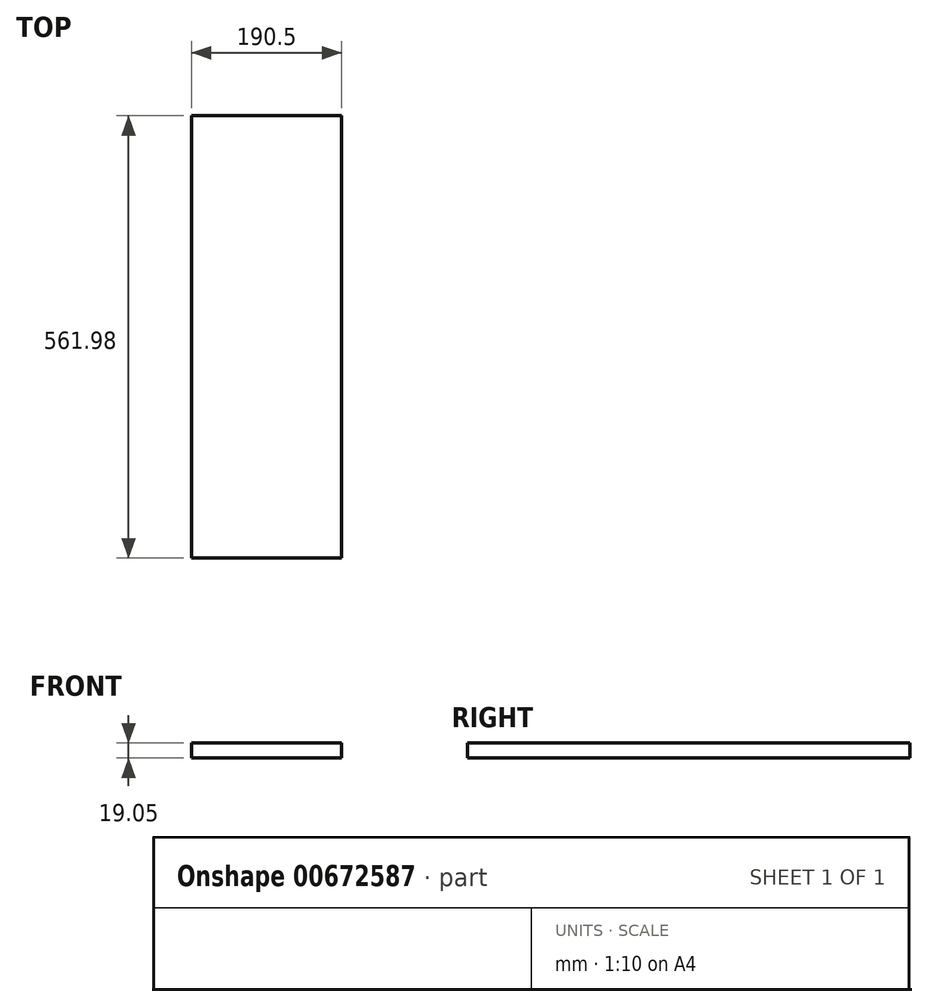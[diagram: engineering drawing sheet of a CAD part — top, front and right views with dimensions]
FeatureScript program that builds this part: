
annotation { "Feature Type Name" : "Feature", "Feature Type Description" : "" }
export const myFeature = defineFeature(function(context is Context, id is Id, definition is map)
    precondition{}
    {
        {
            var Q0;
            Q0=qCreatedBy(makeId("Top.planeOp"),FACE);
            var sketch = newSketch(context, id + "F0", { "sketchPlane" : qUnion([Q0])});
            skLineSegment(sketch, "E0.bottom", {"start": v(95.25, 280.99) * mm, "end": v(-95.25, 280.99) * mm});
            skLineSegment(sketch, "E0.top", {"start": v(95.25, -280.99) * mm, "end": v(-95.25, -280.99) * mm});
            skLineSegment(sketch, "E0.left", {"start": v(95.25, 280.99) * mm, "end": v(95.25, -280.99) * mm});
            skLineSegment(sketch, "E0.right", {"start": v(-95.25, 280.99) * mm, "end": v(-95.25, -280.99) * mm});
            skPoint(sketch, "E0.middle", {"position": v(0, 0) * mm});
            skSolve(sketch);
        }
        {
            var Q0;
            Q0=makeQuery(id+"F0.imprint","IMPRINT",FACE,{"disambiguationData":[TD([[makeQuery(id+"F0.imprint","IMPRINT",EDGE,{"derivedFrom":sQuery(id+"F0.wireOp",EDGE,"E0.bottom")}),1.0]])]});
            extrude(context, id + "F1", {"entities" : qUnion([Q0]), "depth" : 19.05 * mm, "offsetDistance" : 25.4 * mm});
        }
    });
